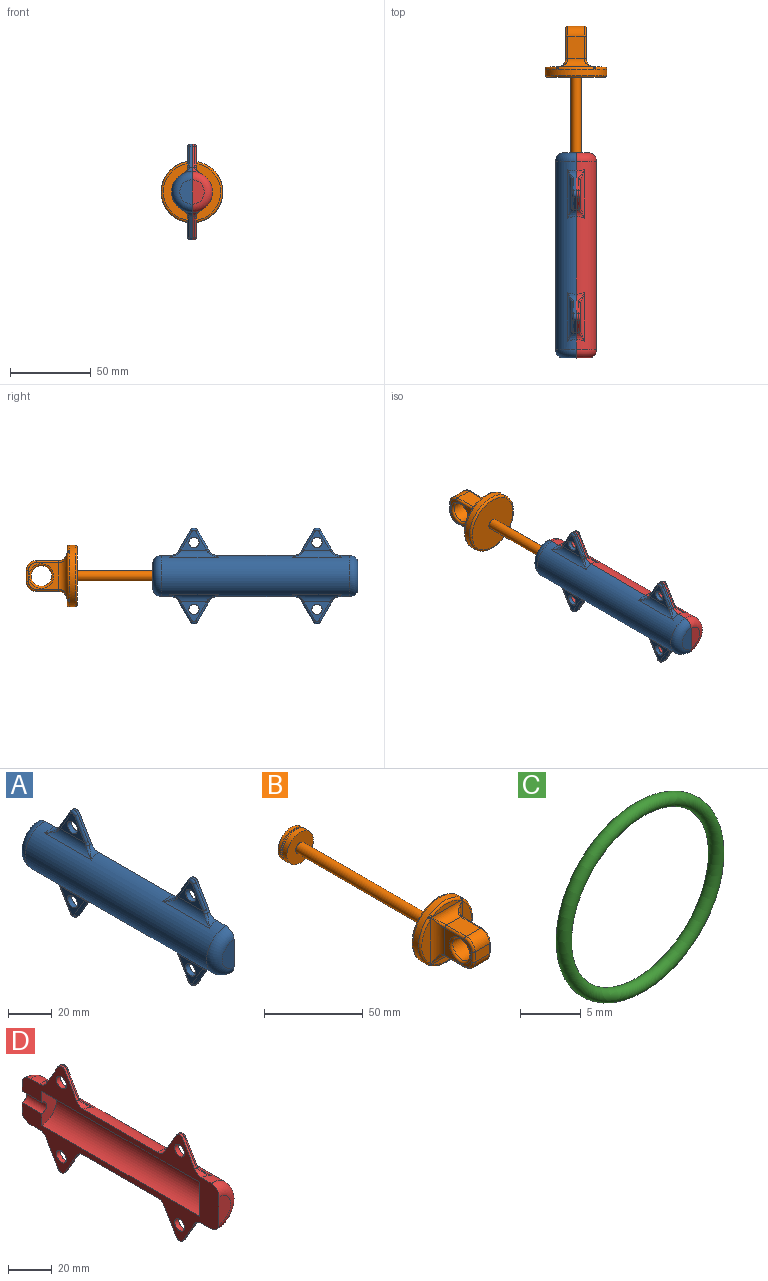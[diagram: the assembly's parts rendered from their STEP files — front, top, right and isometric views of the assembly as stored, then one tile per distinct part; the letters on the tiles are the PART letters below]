
ASSEMBLY  parts=4 mates=4
PART A: 70 faces, bbox 13.8x127x59.7 mm
  f0: cylinder r=12.7mm len=116.84mm, axis (0,1,0), area 4001.9mm2, adj f23,f24,f25,f26,f27,f28,f29,f30
  f1: cylinder r=9.53mm len=101.6mm, axis (0,1,0), area 3040.2mm2, adj f5,f6,f69
  f2: plane 15.24x7.62mm, normal (0,-1,0), area 91.2mm2, adj f32,f69
  f3: plane 15.24x7.62mm, normal (0,1,0), area 75.4mm2, adj f4,f31,f69
  f4: cylinder r=3.17mm len=12.7mm, axis (0,1,0), area 126.7mm2, adj f3,f5,f69
  f5: plane 19.05x9.53mm, normal (0,-1,0), area 126.7mm2, adj f1,f4,f69
  f6: plane 19.05x9.53mm, normal (0,1,0), area 142.5mm2, adj f1,f69
  f7: plane 13.17x7.6mm, normal (0,0.87,0.5), area 19.3mm2, adj f8,f27,f63,f64,f69
  f8: cylinder r=2.54mm len=4.4mm, axis (-1,0,0), area 6.8mm2, adj f7,f9,f65,f69
  f9: plane 13.17x7.6mm, normal (0,-0.87,0.5), area 19.3mm2, adj f8,f28,f66,f67,f69
  f10: cylinder r=3.17mm len=6.35mm, axis (-1,0,0), area 50.7mm2, adj f36,f69
  f11: plane 13.17x7.6mm, normal (0,0.87,0.5), area 19.3mm2, adj f12,f25,f45,f46,f69
  f12: cylinder r=2.54mm len=4.4mm, axis (-1,0,0), area 6.8mm2, adj f11,f13,f44,f69
  f13: plane 13.17x7.6mm, normal (0,-0.87,0.5), area 19.3mm2, adj f12,f26,f42,f43,f69
  f14: cylinder r=3.17mm len=6.35mm, axis (-1,0,0), area 50.7mm2, adj f35,f69
  f15: cylinder r=2.54mm len=4.4mm, axis (-1,0,0), area 6.8mm2, adj f16,f17,f58,f69
  f16: plane 13.17x7.6mm, normal (0,0.87,-0.5), area 19.3mm2, adj f15,f24,f59,f60,f69
  f17: plane 13.17x7.6mm, normal (0,-0.87,-0.5), area 19.3mm2, adj f15,f23,f56,f57,f69
  f18: cylinder r=3.17mm len=6.35mm, axis (-1,0,0), area 50.7mm2, adj f34,f69
  f19: cylinder r=2.54mm len=4.4mm, axis (-1,0,0), area 6.8mm2, adj f20,f21,f51,f69
  f20: plane 13.17x7.6mm, normal (0,0.87,-0.5), area 19.3mm2, adj f19,f30,f52,f53,f69
  f21: plane 13.17x7.6mm, normal (0,-0.87,-0.5), area 19.3mm2, adj f19,f29,f49,f50,f69
  f22: cylinder r=3.17mm len=6.35mm, axis (-1,0,0), area 50.7mm2, adj f33,f69
  f23: bspline ~7.62x5.39mm, area 16.8mm2, adj f0,f17,f55,f69
  f24: bspline ~7.62x5.39mm, area 16.8mm2, adj f0,f16,f61,f69
  f25: bspline ~7.62x5.39mm, area 16.8mm2, adj f0,f11,f47,f69
  f26: bspline ~7.62x5.39mm, area 16.8mm2, adj f0,f13,f41,f69
  f27: bspline ~7.62x5.39mm, area 16.8mm2, adj f0,f7,f62,f69
  f28: bspline ~7.62x5.39mm, area 16.8mm2, adj f0,f9,f68,f69
  f29: bspline ~7.62x5.39mm, area 16.8mm2, adj f0,f21,f48,f69
  f30: bspline ~7.62x5.39mm, area 16.8mm2, adj f0,f20,f54,f69
  f31: torus R=7.62mm, axis (0,-1,0), area 272.1mm2, adj f0,f3,f69
  f32: torus R=7.62mm, axis (0,-1,0), area 272.1mm2, adj f0,f2,f69
  f33: plane 15.65x12.28mm, normal (-1,0,0), area 73.3mm2, adj f22,f40,f50,f51,f52
  f34: plane 15.65x12.28mm, normal (-1,0,0), area 73.3mm2, adj f18,f37,f57,f58,f59
  f35: plane 15.65x12.28mm, normal (-1,0,0), area 73.3mm2, adj f14,f38,f43,f44,f45
  f36: plane 15.65x12.28mm, normal (-1,0,0), area 73.3mm2, adj f10,f39,f64,f65,f66
  f37: cylinder r=5.08mm len=30.31mm, axis (0,1,0), area 127.7mm2, adj f0,f34,f55,f56,f60,f61
  f38: cylinder r=5.08mm len=30.31mm, axis (0,1,0), area 127.7mm2, adj f0,f35,f41,f42,f46,f47
  f39: cylinder r=5.08mm len=30.31mm, axis (0,1,0), area 127.7mm2, adj f0,f36,f62,f63,f67,f68
  f40: cylinder r=5.08mm len=30.31mm, axis (0,1,0), area 127.7mm2, adj f0,f33,f48,f49,f53,f54
  f41: bspline ~6.91x4.57mm, area 4.8mm2, adj f26,f38,f42
  f42: bspline ~1.98x1.85mm, area 3.1mm2, adj f13,f38,f41,f43
  f43: cylinder r=1.27mm len=12.28mm, axis (0,0.5,0.87), area 26.8mm2, adj f13,f35,f42,f44
  f44: torus R=1.27mm, axis (-1,0,0), area 8.7mm2, adj f12,f35,f43,f45
  f45: cylinder r=1.27mm len=12.28mm, axis (0,0.5,-0.87), area 26.8mm2, adj f11,f35,f44,f46
  f46: bspline ~1.98x1.85mm, area 3.1mm2, adj f11,f38,f45,f47
  f47: bspline ~6.91x4.57mm, area 4.8mm2, adj f25,f38,f46
  f48: bspline ~6.91x4.57mm, area 4.8mm2, adj f29,f40,f49
  f49: bspline ~1.98x1.85mm, area 3.1mm2, adj f21,f40,f48,f50
  f50: cylinder r=1.27mm len=12.28mm, axis (0,-0.5,0.87), area 26.8mm2, adj f21,f33,f49,f51
  f51: torus R=1.27mm, axis (-1,0,0), area 8.7mm2, adj f19,f33,f50,f52
  f52: cylinder r=1.27mm len=12.28mm, axis (0,-0.5,-0.87), area 26.8mm2, adj f20,f33,f51,f53
  f53: bspline ~1.98x1.85mm, area 3.1mm2, adj f20,f40,f52,f54
  f54: bspline ~6.91x4.57mm, area 4.8mm2, adj f30,f40,f53
  f55: bspline ~6.91x4.57mm, area 4.8mm2, adj f23,f37,f56
  f56: bspline ~1.98x1.85mm, area 3.1mm2, adj f17,f37,f55,f57
  f57: cylinder r=1.27mm len=12.28mm, axis (0,-0.5,0.87), area 26.8mm2, adj f17,f34,f56,f58
  f58: torus R=1.27mm, axis (-1,0,0), area 8.7mm2, adj f15,f34,f57,f59
  f59: cylinder r=1.27mm len=12.28mm, axis (0,-0.5,-0.87), area 26.8mm2, adj f16,f34,f58,f60
  f60: bspline ~1.98x1.85mm, area 3.1mm2, adj f16,f37,f59,f61
  f61: bspline ~6.91x4.57mm, area 4.8mm2, adj f24,f37,f60
  f62: bspline ~6.91x4.57mm, area 4.8mm2, adj f27,f39,f63
  f63: bspline ~1.98x1.85mm, area 3.1mm2, adj f7,f39,f62,f64
  f64: cylinder r=1.27mm len=12.28mm, axis (0,0.5,-0.87), area 26.8mm2, adj f7,f36,f63,f65
  f65: torus R=1.27mm, axis (-1,0,0), area 8.7mm2, adj f8,f36,f64,f66
  f66: cylinder r=1.27mm len=12.28mm, axis (0,0.5,0.87), area 26.8mm2, adj f9,f36,f65,f67
  f67: bspline ~1.98x1.85mm, area 3.1mm2, adj f9,f39,f66,f68
  f68: bspline ~6.91x4.57mm, area 4.8mm2, adj f28,f39,f67
  f69: plane 127.05x59.28mm, normal (1,0,0), area 1928.6mm2, adj f0,f1,f2,f3,f4,f5,f6,f7
PART B: 58 faces, bbox 41.2x137x41.2 mm
  f0: plane 20.28x3.18mm, normal (0,-1,0), area 43.8mm2, adj f23,f52
  f1: plane 27.24x6.35mm, normal (0,-1,0), area 120.2mm2, adj f25,f44
  f2: plane 20.28x3.18mm, normal (0,-1,0), area 43.8mm2, adj f24,f47
  f3: cylinder r=9.53mm len=19.05mm, axis (0,1,0), area 114mm2, adj f4,f5
  f4: plane 19.05x19.05mm, normal (0,1,0), area 285mm2, adj f3
  f5: plane 19.05x19.05mm, normal (0,-1,0), area 36.7mm2, adj f3,f9
  f6: plane 19.05x19.05mm, normal (0,1,0), area 36.7mm2, adj f8,f9
  f7: plane 19.05x19.05mm, normal (0,-1,0), area 253.4mm2, adj f8,f10
  f8: cylinder r=9.53mm len=19.05mm, axis (0,1,0), area 190mm2, adj f6,f7
  f9: torus R=8.89mm, axis (0,-1,0), area 106.4mm2, adj f5,f6
  f10: cylinder r=3.17mm len=98.43mm, axis (0,1,0), area 1963.5mm2, adj f7,f13
  f11: cylinder r=19.05mm len=38.1mm, axis (0,1,0), area 456.1mm2, adj f41,f42,f44,f45,f46,f47,f49,f50
  f12: plane 27.24x6.35mm, normal (0,-1,0), area 120.2mm2, adj f22,f55
  f13: plane 35.56x35.56mm, normal (0,1,0), area 961.5mm2, adj f10,f41
  f14: plane 13.97x10.16mm, normal (0,0,1), area 141.9mm2, adj f15,f23,f28,f35
  f15: cylinder r=6.35mm len=10.16mm, axis (-1,0,0), area 101.3mm2, adj f14,f16,f30,f37
  f16: plane 10.16x6.35mm, normal (0,-1,0), area 64.5mm2, adj f15,f17,f32,f39
  f17: cylinder r=6.35mm len=10.16mm, axis (-1,0,0), area 101.3mm2, adj f16,f19,f31,f38
  f18: cylinder r=6.35mm len=12.7mm, axis (-1,0,0), area 456mm2, adj f20,f40
  f19: plane 13.97x10.16mm, normal (0,0,-1), area 141.9mm2, adj f17,f24,f29,f36
  f20: plane 19.05x16.51mm, normal (1,0,0), area 176.8mm2, adj f18,f22,f35,f36,f37,f38,f39
  f21: plane 19.05x16.51mm, normal (-1,0,0), area 121mm2, adj f25,f28,f29,f30,f31,f32,f40
  f22: cylinder r=5.08mm len=28.12mm, axis (0,0,1), area 168.1mm2, adj f12,f20,f33,f34,f53,f57
  f23: cylinder r=5.08mm len=21.77mm, axis (-1,0,0), area 117.3mm2, adj f0,f14,f26,f33,f50,f54
  f24: cylinder r=5.08mm len=21.77mm, axis (-1,0,0), area 117.3mm2, adj f2,f19,f27,f34,f45,f49
  f25: cylinder r=5.08mm len=28.12mm, axis (0,0,-1), area 168.1mm2, adj f1,f21,f26,f27,f42,f46
  f26: bspline ~6.35x6.35mm, area 11.4mm2, adj f23,f25,f28,f48
  f27: bspline ~6.35x6.35mm, area 11.4mm2, adj f24,f25,f29,f43
  f28: cylinder r=1.27mm len=13.97mm, axis (0,-1,0), area 27.9mm2, adj f14,f21,f26,f30
  f29: cylinder r=1.27mm len=13.97mm, axis (0,1,0), area 27.9mm2, adj f19,f21,f27,f31
  f30: torus R=5.08mm, axis (1,0,0), area 18.5mm2, adj f15,f21,f28,f32
  f31: torus R=5.08mm, axis (1,0,0), area 18.5mm2, adj f17,f21,f29,f32
  f32: cylinder r=1.27mm len=6.35mm, axis (0,0,-1), area 12.7mm2, adj f16,f21,f30,f31
  f33: bspline ~6.35x6.35mm, area 11.4mm2, adj f22,f23,f35,f56
  f34: bspline ~6.35x6.35mm, area 11.4mm2, adj f22,f24,f36,f51
  f35: cylinder r=1.27mm len=13.97mm, axis (0,1,0), area 27.9mm2, adj f14,f20,f33,f37
  f36: cylinder r=1.27mm len=13.97mm, axis (0,-1,0), area 27.9mm2, adj f19,f20,f34,f38
  f37: torus R=5.08mm, axis (1,0,0), area 18.5mm2, adj f15,f20,f35,f39
  f38: torus R=5.08mm, axis (1,0,0), area 18.5mm2, adj f17,f20,f36,f39
  f39: cylinder r=1.27mm len=6.35mm, axis (0,0,1), area 12.7mm2, adj f16,f20,f37,f38
  f40: torus R=7.62mm, axis (1,0,0), area 85.4mm2, adj f18,f21
  f41: torus R=17.78mm, axis (0,-1,0), area 233mm2, adj f11,f13
  f42: bspline ~3.61x3.58mm, area 1.3mm2, adj f11,f25,f43,f44
  f43: sphere r=1.27mm, area 0.2mm2, adj f27,f42,f45
  f44: torus R=17.78mm, axis (0,-1,0), area 64.7mm2, adj f1,f11,f42,f46
  f45: bspline ~4.61x3.5mm, area 1.8mm2, adj f11,f24,f43,f47
  f46: bspline ~3.29x3.27mm, area 1.3mm2, adj f11,f25,f44,f48
  f47: torus R=17.78mm, axis (0,-1,0), area 45mm2, adj f2,f11,f45,f49
  f48: sphere r=1.27mm, area 0.2mm2, adj f26,f46,f50
  f49: bspline ~3.99x3.08mm, area 1.8mm2, adj f11,f24,f47,f51
  f50: bspline ~2.89x2.36mm, area 1.8mm2, adj f11,f23,f48,f52
  f51: sphere r=1.27mm, area 0.2mm2, adj f34,f49,f53
  f52: torus R=17.78mm, axis (0,-1,0), area 45mm2, adj f0,f11,f50,f54
  f53: bspline ~3.29x3.27mm, area 1.3mm2, adj f11,f22,f51,f55
  f54: bspline ~4.61x3.5mm, area 1.8mm2, adj f11,f23,f52,f56
  f55: torus R=17.78mm, axis (0,-1,0), area 64.7mm2, adj f11,f12,f53,f57
  f56: sphere r=1.27mm, area 0.2mm2, adj f33,f54,f57
  f57: bspline ~3.61x3.58mm, area 1.3mm2, adj f11,f22,f55,f56
PART C: 1 faces, bbox 20.6x1.3x20.6 mm
  f0: torus R=8.89mm, axis (0,-1,0), area 222.9mm2
PART D: 70 faces, bbox 13.8x127x59.7 mm
  f0: cylinder r=5.08mm len=30.31mm, axis (0,1,0), area 127.7mm2, adj f4,f7,f10,f36,f37,f68
  f1: cylinder r=5.08mm len=30.31mm, axis (0,1,0), area 127.7mm2, adj f11,f14,f17,f34,f35,f68
  f2: cylinder r=5.08mm len=30.31mm, axis (0,1,0), area 127.7mm2, adj f27,f28,f29,f38,f39,f68
  f3: cylinder r=5.08mm len=30.31mm, axis (0,1,0), area 127.7mm2, adj f20,f21,f22,f32,f33,f68
  f4: bspline ~1.98x1.85mm, area 3.1mm2, adj f0,f5,f36,f44
  f5: cylinder r=1.27mm len=12.28mm, axis (0,0.5,-0.87), area 26.8mm2, adj f4,f6,f7,f44
  f6: torus R=1.27mm, axis (1,0,0), area 8.7mm2, adj f5,f7,f9,f43
  f7: plane 15.65x12.28mm, normal (1,0,0), area 73.3mm2, adj f0,f5,f6,f8,f9
  f8: cylinder r=3.17mm len=6.35mm, axis (-1,0,0), area 50.7mm2, adj f7,f69
  f9: cylinder r=1.27mm len=12.28mm, axis (0,0.5,0.87), area 26.8mm2, adj f6,f7,f10,f42
  f10: bspline ~1.98x1.85mm, area 3.1mm2, adj f0,f9,f37,f42
  f11: bspline ~1.98x1.85mm, area 3.1mm2, adj f1,f12,f34,f49
  f12: cylinder r=1.27mm len=12.28mm, axis (0,0.5,-0.87), area 26.8mm2, adj f11,f13,f14,f49
  f13: torus R=1.27mm, axis (1,0,0), area 8.7mm2, adj f12,f14,f16,f48
  f14: plane 15.65x12.28mm, normal (1,0,0), area 73.3mm2, adj f1,f12,f13,f15,f16
  f15: cylinder r=3.17mm len=6.35mm, axis (-1,0,0), area 50.7mm2, adj f14,f69
  f16: cylinder r=1.27mm len=12.28mm, axis (0,0.5,0.87), area 26.8mm2, adj f13,f14,f17,f47
  f17: bspline ~1.98x1.85mm, area 3.1mm2, adj f1,f16,f35,f47
  f18: torus R=1.27mm, axis (1,0,0), area 8.7mm2, adj f19,f22,f24,f65
  f19: cylinder r=1.27mm len=12.28mm, axis (0,-0.5,-0.87), area 26.8mm2, adj f18,f20,f22,f64
  f20: bspline ~1.98x1.85mm, area 3.1mm2, adj f3,f19,f33,f64
  f21: bspline ~1.98x1.85mm, area 3.1mm2, adj f3,f24,f32,f62
  f22: plane 15.65x12.28mm, normal (1,0,0), area 73.3mm2, adj f3,f18,f19,f23,f24
  f23: cylinder r=3.17mm len=6.35mm, axis (-1,0,0), area 50.7mm2, adj f22,f69
  f24: cylinder r=1.27mm len=12.28mm, axis (0,-0.5,0.87), area 26.8mm2, adj f18,f21,f22,f62
  f25: torus R=1.27mm, axis (1,0,0), area 8.7mm2, adj f26,f29,f31,f60
  f26: cylinder r=1.27mm len=12.28mm, axis (0,-0.5,-0.87), area 26.8mm2, adj f25,f27,f29,f59
  f27: bspline ~1.98x1.85mm, area 3.1mm2, adj f2,f26,f39,f59
  f28: bspline ~1.98x1.85mm, area 3.1mm2, adj f2,f31,f38,f57
  f29: plane 15.65x12.28mm, normal (1,0,0), area 73.3mm2, adj f2,f25,f26,f30,f31
  f30: cylinder r=3.17mm len=6.35mm, axis (-1,0,0), area 50.7mm2, adj f29,f69
  f31: cylinder r=1.27mm len=12.28mm, axis (0,-0.5,0.87), area 26.8mm2, adj f25,f28,f29,f57
  f32: bspline ~6.91x4.57mm, area 4.8mm2, adj f3,f21,f61
  f33: bspline ~6.91x4.57mm, area 4.8mm2, adj f3,f20,f63
  f34: bspline ~6.91x4.57mm, area 4.8mm2, adj f1,f11,f45
  f35: bspline ~6.91x4.57mm, area 4.8mm2, adj f1,f17,f46
  f36: bspline ~6.91x4.57mm, area 4.8mm2, adj f0,f4,f40
  f37: bspline ~6.91x4.57mm, area 4.8mm2, adj f0,f10,f41
  f38: bspline ~6.91x4.57mm, area 4.8mm2, adj f2,f28,f56
  f39: bspline ~6.91x4.57mm, area 4.8mm2, adj f2,f27,f58
  f40: bspline ~7.62x5.39mm, area 16.8mm2, adj f36,f44,f68,f69
  f41: bspline ~7.62x5.39mm, area 16.8mm2, adj f37,f42,f68,f69
  f42: plane 13.17x7.6mm, normal (0,-0.87,0.5), area 19.3mm2, adj f9,f10,f41,f43,f69
  f43: cylinder r=2.54mm len=4.4mm, axis (-1,0,0), area 6.8mm2, adj f6,f42,f44,f69
  f44: plane 13.17x7.6mm, normal (0,0.87,0.5), area 19.3mm2, adj f4,f5,f40,f43,f69
  f45: bspline ~7.62x5.39mm, area 16.8mm2, adj f34,f49,f68,f69
  f46: bspline ~7.62x5.39mm, area 16.8mm2, adj f35,f47,f68,f69
  f47: plane 13.17x7.6mm, normal (0,-0.87,0.5), area 19.3mm2, adj f16,f17,f46,f48,f69
  f48: cylinder r=2.54mm len=4.4mm, axis (-1,0,0), area 6.8mm2, adj f13,f47,f49,f69
  f49: plane 13.17x7.6mm, normal (0,0.87,0.5), area 19.3mm2, adj f11,f12,f45,f48,f69
  f50: plane 19.05x9.53mm, normal (0,-1,0), area 126.7mm2, adj f51,f55,f69
  f51: cylinder r=3.17mm len=12.7mm, axis (0,1,0), area 126.7mm2, adj f50,f53,f69
  f52: torus R=7.62mm, axis (0,-1,0), area 272.1mm2, adj f53,f68,f69
  f53: plane 15.24x7.62mm, normal (0,1,0), area 75.4mm2, adj f51,f52,f69
  f54: plane 19.05x9.53mm, normal (0,1,0), area 142.5mm2, adj f55,f69
  f55: cylinder r=9.53mm len=101.6mm, axis (0,1,0), area 3040.2mm2, adj f50,f54,f69
  f56: bspline ~7.62x5.39mm, area 16.8mm2, adj f38,f57,f68,f69
  f57: plane 13.17x7.6mm, normal (0,-0.87,-0.5), area 19.3mm2, adj f28,f31,f56,f60,f69
  f58: bspline ~7.62x5.39mm, area 16.8mm2, adj f39,f59,f68,f69
  f59: plane 13.17x7.6mm, normal (0,0.87,-0.5), area 19.3mm2, adj f26,f27,f58,f60,f69
  f60: cylinder r=2.54mm len=4.4mm, axis (-1,0,0), area 6.8mm2, adj f25,f57,f59,f69
  f61: bspline ~7.62x5.39mm, area 16.8mm2, adj f32,f62,f68,f69
  f62: plane 13.17x7.6mm, normal (0,-0.87,-0.5), area 19.3mm2, adj f21,f24,f61,f65,f69
  f63: bspline ~7.62x5.39mm, area 16.8mm2, adj f33,f64,f68,f69
  f64: plane 13.17x7.6mm, normal (0,0.87,-0.5), area 19.3mm2, adj f19,f20,f63,f65,f69
  f65: cylinder r=2.54mm len=4.4mm, axis (-1,0,0), area 6.8mm2, adj f18,f62,f64,f69
  f66: torus R=7.62mm, axis (0,-1,0), area 272.1mm2, adj f67,f68,f69
  f67: plane 15.24x7.62mm, normal (0,-1,0), area 91.2mm2, adj f66,f69
  f68: cylinder r=12.7mm len=116.84mm, axis (0,1,0), area 4001.9mm2, adj f0,f1,f2,f3,f40,f41,f45,f46
  f69: plane 127.05x59.28mm, normal (-1,0,0), area 1928.6mm2, adj f8,f15,f23,f30,f40,f41,f42,f43
PLACE A t=(-26.46,-10.95,14.85)mm
PLACE B rot(axis=(1,0,0),180deg) t=(-26.46,-65.7,14.85)mm
PLACE C rot(axis=(1,0,0),180deg) t=(-26.46,-66.33,14.85)mm
PLACE D t=(-26.46,-10.95,14.85)mm
MATE fastened A.f10 <-> D.f8  axis (1,0,0) through (-26.46,-112.55,35.58)mm
MATE slider A.f1 <-> B.f3  axis (0,1,0) through (-26.46,-74.45,14.85)mm
MATE slider B.f3 <-> A.f1  axis (0,-1,0) through (-26.46,-68.87,14.85)mm
MATE fastened C.f0 <-> B.f9  axis (0,1,0) through (-26.46,-66.33,14.85)mm
